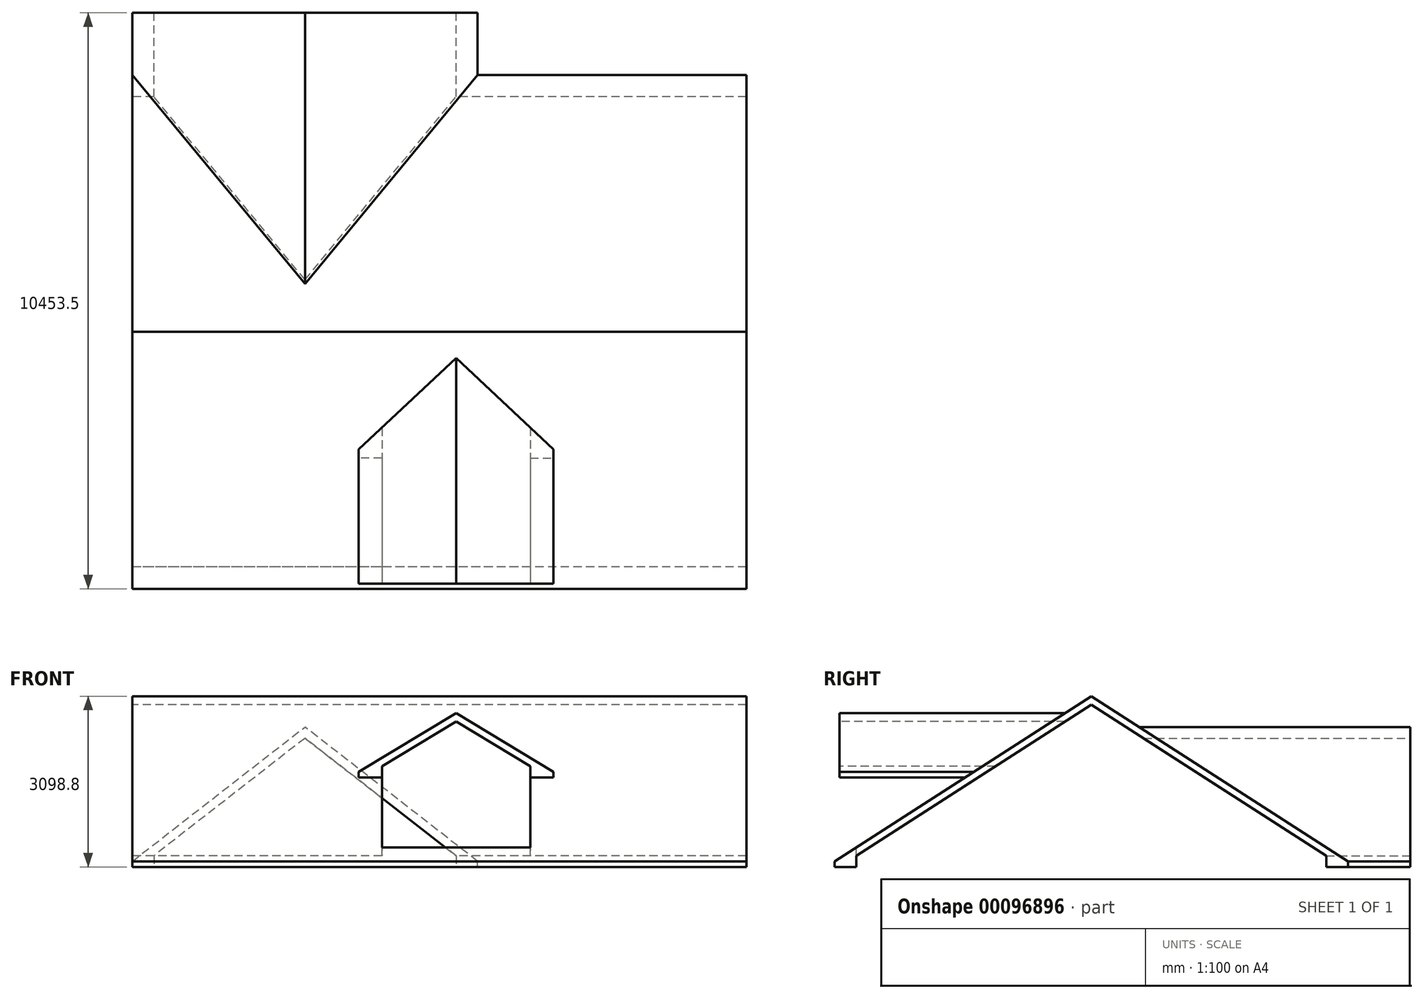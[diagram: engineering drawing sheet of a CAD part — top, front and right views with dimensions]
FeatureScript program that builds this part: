
annotation { "Feature Type Name" : "Feature", "Feature Type Description" : "" }
export const myFeature = defineFeature(function(context is Context, id is Id, definition is map)
    precondition{}
    {
        {
            var Q0;
            Q0=qCreatedBy(makeId("Front.planeOp"),FACE);
            cPlane(context, id + "F0", {"entities" : qUnion([Q0]), "cplaneType" : CPlaneType.OFFSET, "offset" : 4267.2 * mm, "width" : 152.4 * mm, "height" : 152.4 * mm});
        }
        {
            var Q0;
            Q0=qCreatedBy(makeId("Front.planeOp"),FACE);
            cPlane(context, id + "F1", {"entities" : qUnion([Q0]), "cplaneType" : CPlaneType.OFFSET, "offset" : 5486.4 * mm, "oppositeDirection" : true, "width" : 152.4 * mm, "height" : 152.4 * mm});
        }
        {
            var Q0;
            Q0=qCreatedBy(makeId("Right.planeOp"),FACE);
            var sketch = newSketch(context, id + "F2", { "sketchPlane" : qUnion([Q0])});
            skLineSegment(sketch, "E0", {"start": v(-4267.2, 0) * mm, "end": v(4267.2, 0) * mm, "construction": true});
            skLineSegment(sketch, "E1", {"start": v(0, 0) * mm, "end": v(0, 2743.2) * mm, "construction": true});
            skLineSegment(sketch, "E2", {"start": v(0, 2743.2) * mm, "end": v(0, 2895.6) * mm, "construction": true});
            skLineSegment(sketch, "E3", {"start": v(-4267.2, 0) * mm, "end": v(0, 2743.2) * mm});
            skLineSegment(sketch, "E4", {"start": v(0, 2895.6) * mm, "end": v(-4662.31, -101.6) * mm});
            skLineSegment(sketch, "E5", {"start": v(-4267.2, 0) * mm, "end": v(-4267.2, -203.2) * mm});
            skLineSegment(sketch, "E6", {"start": v(-4267.2, -203.2) * mm, "end": v(-4662.31, -203.2) * mm});
            skLineSegment(sketch, "E7", {"start": v(-4662.31, -203.2) * mm, "end": v(-4662.31, -101.6) * mm});
            skLineSegment(sketch, "E8.MirrorCS", {"start": v(0, 2895.6) * mm, "end": v(4662.31, -101.6) * mm});
            skLineSegment(sketch, "E9.MirrorCS", {"start": v(4267.2, 0) * mm, "end": v(0, 2743.2) * mm});
            skLineSegment(sketch, "E10.MirrorCS", {"start": v(4267.2, 0) * mm, "end": v(4267.2, -203.2) * mm});
            skLineSegment(sketch, "E11.MirrorCS", {"start": v(4267.2, -203.2) * mm, "end": v(4662.31, -203.2) * mm});
            skLineSegment(sketch, "E12.MirrorCS", {"start": v(4662.31, -203.2) * mm, "end": v(4662.31, -101.6) * mm});
            skSolve(sketch);
        }
        {
            var Q0;
            Q0 = qSketchRegion(id + "F2", true);
            extrude(context, id + "F3", {"entities" : qUnion([Q0]), "depth" : 11150.6 * mm});
        }
        {
            var Q0;
            Q0=qCreatedBy(id+"F0.planeOp",FACE);
            var sketch = newSketch(context, id + "F4", { "sketchPlane" : qUnion([Q0])});
            skLineSegment(sketch, "E13", {"start": v(5880.1, 0) * mm, "end": v(5880.1, 2438.4) * mm, "construction": true});
            skLineSegment(sketch, "E14", {"start": v(4533.9, 0) * mm, "end": v(7226.3, 0) * mm});
            skLineSegment(sketch, "E15", {"start": v(4533.9, 0) * mm, "end": v(4533.9, 1625.6) * mm});
            skLineSegment(sketch, "E16", {"start": v(4533.9, 1625.6) * mm, "end": v(5880.1, 2438.4) * mm});
            skLineSegment(sketch, "E17.MirrorCS", {"start": v(7226.3, 1625.6) * mm, "end": v(5880.1, 2438.4) * mm});
            skLineSegment(sketch, "E18.MirrorCS", {"start": v(7226.3, 0) * mm, "end": v(7226.3, 1625.6) * mm});
            skSolve(sketch);
        }
        {
            var Q0;
            Q0 = qSketchRegion(id + "F4", true);
            var Q1;
            Q1=makeQuery(id+"F3.opExtrude","SWEPT_FACE",FACE,{"disambiguationData":[OSD([sQuery(id+"F2.wireOp",EDGE,"E3")])]});
            extrude(context, id + "F5", {"entities" : qUnion([Q0]), "operationType" : NewBodyOperationType.REMOVE, "endBound" : BoundingType.UP_TO_SURFACE, "oppositeDirection" : true, "endBoundEntityFace" : qUnion([Q1]), "depth" : 25.4 * mm});
        }
        {
            var Q0;
            Q0=qCreatedBy(id+"F0.planeOp",FACE);
            var sketch = newSketch(context, id + "F6", { "sketchPlane" : qUnion([Q0])});
            skLineSegment(sketch, "E19", {"start": v(5880.1, 0) * mm, "end": v(5880.1, 2438.4) * mm, "construction": true});
            skLineSegment(sketch, "E20", {"start": v(5880.1, 0) * mm, "end": v(4533.9, 0) * mm, "construction": true});
            skLineSegment(sketch, "E21", {"start": v(4533.9, 0) * mm, "end": v(4533.9, 1625.6) * mm, "construction": true});
            skLineSegment(sketch, "E22", {"start": v(4533.9, 1625.6) * mm, "end": v(5880.1, 2438.4) * mm});
            skLineSegment(sketch, "E23", {"start": v(5880.1, 2438.4) * mm, "end": v(5880.1, 2590.8) * mm, "construction": true});
            skLineSegment(sketch, "E24", {"start": v(5880.1, 2590.8) * mm, "end": v(4113.21, 1524) * mm});
            skLineSegment(sketch, "E25", {"start": v(4533.9, 1625.6) * mm, "end": v(4533.9, 1422.4) * mm});
            skLineSegment(sketch, "E26", {"start": v(4533.9, 1422.4) * mm, "end": v(4113.21, 1422.4) * mm});
            skLineSegment(sketch, "E27", {"start": v(4113.21, 1422.4) * mm, "end": v(4113.21, 1524) * mm});
            skLineSegment(sketch, "E28.MirrorCS", {"start": v(7226.3, 1625.6) * mm, "end": v(7226.3, 1422.4) * mm});
            skLineSegment(sketch, "E29.MirrorCS", {"start": v(7226.3, 1422.4) * mm, "end": v(7646.99, 1422.4) * mm});
            skLineSegment(sketch, "E30.MirrorCS", {"start": v(7646.99, 1422.4) * mm, "end": v(7646.99, 1524) * mm});
            skLineSegment(sketch, "E31.MirrorCS", {"start": v(5880.1, 2590.8) * mm, "end": v(7646.99, 1524) * mm});
            skLineSegment(sketch, "E32.MirrorCS", {"start": v(7226.3, 1625.6) * mm, "end": v(5880.1, 2438.4) * mm});
            skSolve(sketch);
        }
        {
            var Q0;
            Q0 = qSketchRegion(id + "F6", true);
            extrude(context, id + "F7", {"entities" : qUnion([Q0]), "operationType" : NewBodyOperationType.ADD, "endBound" : BoundingType.UP_TO_NEXT, "oppositeDirection" : true, "depth" : 25.4 * mm, "hasSecondDirection" : true, "secondDirectionOppositeDirection" : false, "secondDirectionDepth" : 304.8 * mm});
        }
        {
            var Q0;
            Q0=qCreatedBy(id+"F1.planeOp",FACE);
            var sketch = newSketch(context, id + "F8", { "sketchPlane" : qUnion([Q0])});
            skLineSegment(sketch, "E33", {"start": v(3136.9, 0) * mm, "end": v(3136.9, 2133.6) * mm, "construction": true});
            skLineSegment(sketch, "E34", {"start": v(5880.1, 0) * mm, "end": v(393.7, 0) * mm, "construction": true});
            skLineSegment(sketch, "E35", {"start": v(5880.1, 0) * mm, "end": v(5880.1, -203.2) * mm});
            skLineSegment(sketch, "E36", {"start": v(5880.1, 0) * mm, "end": v(3136.9, 2133.6) * mm});
            skLineSegment(sketch, "E37.MirrorCS", {"start": v(393.7, 0) * mm, "end": v(3136.9, 2133.6) * mm});
            skLineSegment(sketch, "E38.MirrorCS", {"start": v(393.7, 0) * mm, "end": v(393.7, -203.2) * mm});
            skLineSegment(sketch, "E39", {"start": v(5880.1, -203.2) * mm, "end": v(393.7, -203.2) * mm});
            skSolve(sketch);
        }
        {
            var Q0;
            Q0 = qSketchRegion(id + "F8", true);
            var Q1;
            Q1=qCreatedBy(makeId("Front.planeOp"),FACE);
            var Q2;
            Q2=makeQuery(id+"F3.opExtrude","SWEPT_FACE",FACE,{"disambiguationData":[OSD([sQuery(id+"F2.wireOp",EDGE,"E9.MirrorCS")])]});
            extrude(context, id + "F9", {"entities" : qUnion([Q0]), "operationType" : NewBodyOperationType.REMOVE, "endBound" : BoundingType.UP_TO_SURFACE, "endBoundEntityFace" : qUnion([Q1]), "depth" : 25.4 * mm});
        }
        {
            var Q0;
            Q0=qCreatedBy(id+"F1.planeOp",FACE);
            var sketch = newSketch(context, id + "F10", { "sketchPlane" : qUnion([Q0])});
            skLineSegment(sketch, "E40", {"start": v(3136.9, 0) * mm, "end": v(3136.9, 2133.6) * mm, "construction": true});
            skLineSegment(sketch, "E41", {"start": v(5880.1, 0) * mm, "end": v(393.7, 0) * mm, "construction": true});
            skLineSegment(sketch, "E42", {"start": v(3136.9, 2133.6) * mm, "end": v(3136.9, 2336.8) * mm, "construction": true});
            skLineSegment(sketch, "E43", {"start": v(5880.1, 0) * mm, "end": v(3136.9, 2133.6) * mm});
            skLineSegment(sketch, "E44", {"start": v(3136.9, 2336.8) * mm, "end": v(6271.99, -101.6) * mm});
            skLineSegment(sketch, "E45", {"start": v(5880.1, 0) * mm, "end": v(5880.1, -203.2) * mm});
            skLineSegment(sketch, "E46", {"start": v(5880.1, -203.2) * mm, "end": v(6271.99, -203.2) * mm});
            skLineSegment(sketch, "E47", {"start": v(6271.99, -203.2) * mm, "end": v(6271.99, -101.6) * mm});
            skLineSegment(sketch, "E48.MirrorCS", {"start": v(393.7, 0) * mm, "end": v(3136.9, 2133.6) * mm});
            skLineSegment(sketch, "E49.MirrorCS", {"start": v(3136.9, 2336.8) * mm, "end": v(1.81, -101.6) * mm});
            skLineSegment(sketch, "E50.MirrorCS", {"start": v(393.7, -203.2) * mm, "end": v(1.81, -203.2) * mm});
            skLineSegment(sketch, "E51.MirrorCS", {"start": v(393.7, 0) * mm, "end": v(393.7, -203.2) * mm});
            skLineSegment(sketch, "E52.MirrorCS", {"start": v(1.81, -203.2) * mm, "end": v(1.81, -101.6) * mm});
            skSolve(sketch);
        }
        {
            var Q0;
            Q0 = qSketchRegion(id + "F10", true);
            extrude(context, id + "F11", {"entities" : qUnion([Q0]), "operationType" : NewBodyOperationType.ADD, "endBound" : BoundingType.UP_TO_NEXT, "depth" : 25.4 * mm, "hasSecondDirection" : true, "secondDirectionOppositeDirection" : true, "secondDirectionDepth" : 304.8 * mm});
        }
    });
